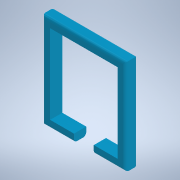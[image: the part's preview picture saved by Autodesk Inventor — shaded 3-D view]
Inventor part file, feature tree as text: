
AUTODESK INVENTOR PART (.ipt)
format: ipt  version: 2020 (Build 240168000, 168)  size: 132,608 bytes
history: native  units: in
note: dims shown in document units (in); Inventor stores cm internally (conversion verified against a paired STEP export)
features: other x10, reference x6, extrude x2, sketch x2, fillet x1
ambient origin geometry x8: Origin, YZ Plane, XZ Plane, XY Plane, X Axis, Y Axis, Z Axis, Center Point
bodies: Solid1 (feature_tree)
feature tree (21):
  extrude  "Extrusion1"  Depth=0.0625in
  fillet  "Fillet1"  Radius=0.0625in
  extrude  "Extrusion2"  Depth=3.25in
  sketch  "Sketch1"  dims[d0=0.0625in d1=0.0625in d2=0.0625in]
  reference  "Reference1"
  reference  "Reference2"
  reference  "Reference3"
  reference  "Reference4"
  sketch  "Sketch2"  dims[d3=0.0625in d4=3.25in d5=5.0in d6=0.0in d7=1.25in d8=0.0in d9=0.0in]
  reference  "Reference5"
  reference  "Reference6"
  other  "<userpath>\Documents\FRC\2020\Prototype1.iam"
  other  "Prototype1.iam"
  other  "DriveBase2020:1"
  other  "AM14U3 End Sheet PowerCell_MIR:1"
  other  "AM14U3 Long Half_1"
  other  "AM14U3 Long Frame Half_3"
  other  "AM14U3 Outside Sheet Rev1_DefaultSM-FLAT-PATTERN_137"
  other  "AM14U3 End Sheet Square:2"
  other  "AM14U3 Long Half:2"
  other  "AM14U3 End Sheet PowerCell:1"
